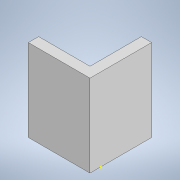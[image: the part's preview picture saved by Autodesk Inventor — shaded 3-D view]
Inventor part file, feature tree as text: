
AUTODESK INVENTOR PART (.ipt)
format: ipt  version: 2020 (Build 240168000, 168)  size: 92,160 bytes
history: native  units: in
note: dims shown in document units (in); Inventor stores cm internally (conversion verified against a paired STEP export)
features: sketch x2, extrude x1
ambient origin geometry x8: Origin, YZ Plane, XZ Plane, XY Plane, X Axis, Y Axis, Z Axis, Center Point
bodies: Solid1 (feature_tree)
feature tree (3):
  extrude  "Extrusion1"  Depth=0.125in
  sketch  "Sketch2"  dims[d2=0.625in d3=0.625in d4=1.0in d5=0.0in]
  sketch  "Sketch1"  dims[d0=0.75in d1=0.125in]
